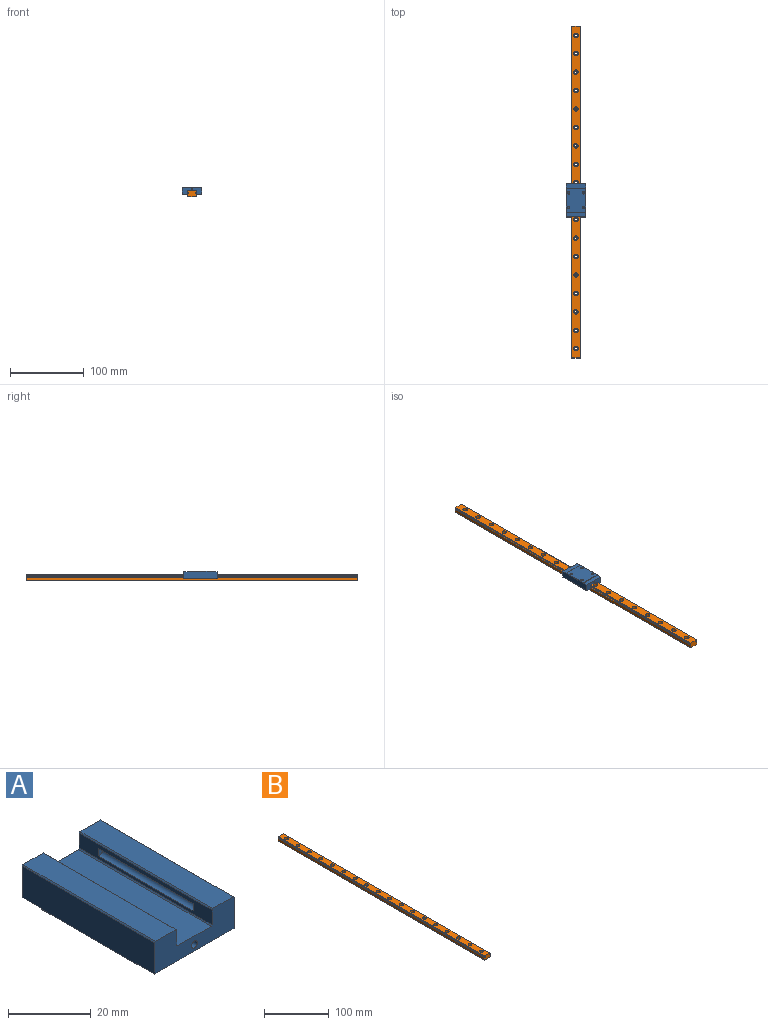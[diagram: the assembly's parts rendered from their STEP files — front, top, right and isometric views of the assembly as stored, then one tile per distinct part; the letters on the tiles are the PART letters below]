
ASSEMBLY  parts=2 mates=1
PART A: 37 faces, bbox 27x45.4x10 mm
  f0: plane 45.4x0.3mm, normal (-0.71,0,0.71), area 19.3mm2, adj f3,f6,f22,f23
  f1: plane 45.4x0.3mm, normal (0.71,0,0.71), area 19.3mm2, adj f10,f11,f22,f23
  f2: plane 45.4x0.3mm, normal (0.71,0,0.71), area 19.3mm2, adj f6,f7,f22,f23
  f3: plane 45.4x4.4mm, normal (-1,0,0), area 129.2mm2, adj f0,f5,f17,f20,f22,f23,f24
  f4: plane 45.4x11.4mm, normal (0,0,1), area 517.6mm2, adj f16,f17,f22,f23
  f5: cylinder r=1.15mm len=32.4mm, axis (0,-1,0), area 141.5mm2, adj f3,f20,f24
  f6: plane 45.4x6.9mm, normal (0,0,1), area 313.3mm2, adj f0,f2,f22,f23
  f7: plane 45.4x9.4mm, normal (1,0,0), area 424.2mm2, adj f2,f15,f18,f21,f22,f23,f25,f35
  f8: plane 32.4x26.4mm, normal (0,0,-1), area 821.1mm2, adj f14,f15,f18,f27,f29,f31,f33,f35
  f9: plane 45.4x9.4mm, normal (-1,0,0), area 424.2mm2, adj f14,f18,f21,f22,f23,f25,f34,f35
  f10: plane 45.4x6.9mm, normal (0,0,1), area 313.3mm2, adj f1,f22,f23,f34
  f11: plane 45.4x4.4mm, normal (1,0,0), area 129.2mm2, adj f1,f12,f16,f19,f22,f23,f36
  f12: cylinder r=1.15mm len=32.4mm, axis (0,-1,0), area 141.5mm2, adj f11,f19,f36
  f13: cylinder r=1mm len=45.4mm, axis (0,-1,0), area 285.3mm2, adj f22,f23
  f14: plane 32.4x0.3mm, normal (-0.71,0,-0.71), area 13.7mm2, adj f8,f9,f18,f35
  f15: plane 32.4x0.3mm, normal (0.71,0,-0.71), area 13.7mm2, adj f7,f8,f18,f35
  f16: plane 45.4x0.3mm, normal (0.71,0,0.71), area 19.3mm2, adj f4,f11,f22,f23
  f17: plane 45.4x0.3mm, normal (-0.71,0,0.71), area 19.3mm2, adj f3,f4,f22,f23
  f18: plane 27x0.5mm, normal (0,-1,0), area 13.4mm2, adj f7,f8,f9,f14,f15,f21
  f19: plane 2.3x1.52mm, normal (0,1,0), area 2.9mm2, adj f11,f12
  f20: plane 2.3x1.52mm, normal (0,1,0), area 2.9mm2, adj f3,f5
  f21: plane 27x6.5mm, normal (0,0,-1), area 175.5mm2, adj f7,f9,f18,f22
  f22: plane 27x9.5mm, normal (0,-1,0), area 193.3mm2, adj f0,f1,f2,f3,f4,f6,f7,f9
  f23: plane 27x9.5mm, normal (0,1,0), area 193.3mm2, adj f0,f1,f2,f3,f4,f6,f7,f9
  f24: plane 2.3x1.52mm, normal (0,-1,0), area 2.9mm2, adj f3,f5
  f25: plane 27x6.5mm, normal (0,0,-1), area 175.5mm2, adj f7,f9,f23,f35
  f26: cone r=857.17mm half-angle=59deg, axis (0,0,-1), area 10mm2, adj f27
  f27: cylinder r=1.65mm len=3.5mm, axis (0,0,1), area 36.3mm2, adj f8,f26
  f28: cone r=857.17mm half-angle=59deg, axis (0,0,-1), area 10mm2, adj f29
  f29: cylinder r=1.65mm len=3.5mm, axis (0,0,1), area 36.3mm2, adj f8,f28
  f30: cone r=857.17mm half-angle=59deg, axis (0,0,-1), area 10mm2, adj f31
  f31: cylinder r=1.65mm len=3.5mm, axis (0,0,1), area 36.3mm2, adj f8,f30
  f32: cone r=857.17mm half-angle=59deg, axis (0,0,-1), area 10mm2, adj f33
  f33: cylinder r=1.65mm len=3.5mm, axis (0,0,1), area 36.3mm2, adj f8,f32
  f34: plane 45.4x0.3mm, normal (-0.71,0,0.71), area 19.3mm2, adj f9,f10,f22,f23
  f35: plane 27x0.5mm, normal (0,1,0), area 13.4mm2, adj f7,f8,f9,f14,f15,f25
  f36: plane 2.3x1.52mm, normal (0,-1,0), area 2.9mm2, adj f11,f12
PART B: 76 faces, bbox 12x450x8 mm
  f0: plane 450x0.51mm, normal (0,0,1), area 229.4mm2, adj f1,f19,f20,f51
  f1: plane 450x0.3mm, normal (1,0,0), area 135mm2, adj f0,f2,f20,f51
  f2: plane 450x0.51mm, normal (0,0,-1), area 229.4mm2, adj f1,f3,f20,f51
  f3: cylinder r=1.15mm len=450mm, axis (0,1,0), area 575.7mm2, adj f2,f4,f20,f51
  f4: plane 450x0.86mm, normal (1,0,0), area 387.4mm2, adj f3,f5,f20,f51
  f5: plane 450x0.35mm, normal (0.71,0,0.71), area 222.7mm2, adj f4,f6,f20,f51
  f6: plane 450x11.3mm, normal (0,0,1), area 4576.1mm2, adj f5,f7,f20,f23,f26,f29,f32,f35
  f7: plane 450x0.35mm, normal (-0.71,0,0.71), area 222.7mm2, adj f6,f8,f20,f51
  f8: plane 450x0.86mm, normal (-1,0,0), area 387.4mm2, adj f7,f9,f20,f51
  f9: cylinder r=1.15mm len=450mm, axis (0,1,0), area 575.7mm2, adj f8,f10,f20,f51
  f10: plane 450x0.51mm, normal (0,0,-1), area 229.4mm2, adj f9,f11,f20,f51
  f11: plane 450x0.3mm, normal (-1,0,0), area 135mm2, adj f10,f12,f20,f51
  f12: plane 450x0.51mm, normal (0,0,1), area 229.4mm2, adj f11,f13,f20,f51
  f13: cylinder r=1.15mm len=450mm, axis (0,1,0), area 575.7mm2, adj f12,f14,f20,f51
  f14: plane 450x4.26mm, normal (-1,0,0), area 1917.6mm2, adj f13,f15,f20,f51
  f15: plane 450x0.35mm, normal (-0.71,0,-0.71), area 222.7mm2, adj f14,f16,f20,f51
  f16: plane 450x11.3mm, normal (0,0,-1), area 4911.8mm2, adj f15,f17,f20,f21,f24,f27,f30,f33
  f17: plane 450x0.35mm, normal (0.71,0,-0.71), area 222.7mm2, adj f16,f18,f20,f51
  f18: plane 450x4.26mm, normal (1,0,0), area 1917.6mm2, adj f17,f19,f20,f51
  f19: cylinder r=1.15mm len=450mm, axis (0,1,0), area 575.7mm2, adj f0,f18,f20,f51
  f20: plane 12x8mm, normal (0,-1,0), area 93mm2, adj f0,f1,f2,f3,f4,f5,f6,f7
  f21: cylinder r=1.75mm len=3.5mm, axis (0,0,1), area 38.5mm2, adj f16,f22
  f22: plane 6x6mm, normal (0,0,1), area 18.7mm2, adj f21,f23
  f23: cylinder r=3mm len=6mm, axis (0,0,1), area 84.8mm2, adj f6,f22
  f24: cylinder r=1.75mm len=3.5mm, axis (0,0,1), area 38.5mm2, adj f16,f25
  f25: plane 6x6mm, normal (0,0,1), area 18.7mm2, adj f24,f26
  f26: cylinder r=3mm len=6mm, axis (0,0,1), area 84.8mm2, adj f6,f25
  f27: cylinder r=1.75mm len=3.5mm, axis (0,0,1), area 38.5mm2, adj f16,f28
  f28: plane 6x6mm, normal (0,0,1), area 18.7mm2, adj f27,f29
  f29: cylinder r=3mm len=6mm, axis (0,0,1), area 84.8mm2, adj f6,f28
  f30: cylinder r=1.75mm len=3.5mm, axis (0,0,1), area 38.5mm2, adj f16,f31
  f31: plane 6x6mm, normal (0,0,1), area 18.7mm2, adj f30,f32
  f32: cylinder r=3mm len=6mm, axis (0,0,1), area 84.8mm2, adj f6,f31
  f33: cylinder r=1.75mm len=3.5mm, axis (0,0,1), area 38.5mm2, adj f16,f34
  f34: plane 6x6mm, normal (0,0,1), area 18.7mm2, adj f33,f35
  f35: cylinder r=3mm len=6mm, axis (0,0,1), area 84.8mm2, adj f6,f34
  f36: cylinder r=1.75mm len=3.5mm, axis (0,0,1), area 38.5mm2, adj f16,f37
  f37: plane 6x6mm, normal (0,0,1), area 18.7mm2, adj f36,f38
  f38: cylinder r=3mm len=6mm, axis (0,0,1), area 84.8mm2, adj f6,f37
  f39: cylinder r=1.75mm len=3.5mm, axis (0,0,1), area 38.5mm2, adj f16,f40
  f40: plane 6x6mm, normal (0,0,1), area 18.7mm2, adj f39,f41
  f41: cylinder r=3mm len=6mm, axis (0,0,1), area 84.8mm2, adj f6,f40
  f42: cylinder r=1.75mm len=3.5mm, axis (0,0,1), area 38.5mm2, adj f16,f43
  f43: plane 6x6mm, normal (0,0,1), area 18.7mm2, adj f42,f44
  f44: cylinder r=3mm len=6mm, axis (0,0,1), area 84.8mm2, adj f6,f43
  f45: cylinder r=1.75mm len=3.5mm, axis (0,0,1), area 38.5mm2, adj f16,f46
  f46: plane 6x6mm, normal (0,0,1), area 18.7mm2, adj f45,f47
  f47: cylinder r=3mm len=6mm, axis (0,0,1), area 84.8mm2, adj f6,f46
  f48: cylinder r=1.75mm len=3.5mm, axis (0,0,1), area 38.5mm2, adj f16,f49
  f49: plane 6x6mm, normal (0,0,1), area 18.7mm2, adj f48,f50
  f50: cylinder r=3mm len=6mm, axis (0,0,1), area 84.8mm2, adj f6,f49
  f51: plane 12x8mm, normal (0,1,0), area 93mm2, adj f0,f1,f2,f3,f4,f5,f6,f7
  f52: cylinder r=1.75mm len=3.5mm, axis (0,0,1), area 38.5mm2, adj f16,f53
  f53: plane 6x6mm, normal (0,0,1), area 18.7mm2, adj f52,f54
  f54: cylinder r=3mm len=6mm, axis (0,0,1), area 84.8mm2, adj f6,f53
  f55: cylinder r=1.75mm len=3.5mm, axis (0,0,1), area 38.5mm2, adj f16,f56
  f56: plane 6x6mm, normal (0,0,1), area 18.7mm2, adj f55,f57
  f57: cylinder r=3mm len=6mm, axis (0,0,1), area 84.8mm2, adj f6,f56
  f58: cylinder r=1.75mm len=3.5mm, axis (0,0,1), area 38.5mm2, adj f16,f59
  f59: plane 6x6mm, normal (0,0,1), area 18.7mm2, adj f58,f60
  f60: cylinder r=3mm len=6mm, axis (0,0,1), area 84.8mm2, adj f6,f59
  f61: cylinder r=1.75mm len=3.5mm, axis (0,0,1), area 38.5mm2, adj f16,f62
  f62: plane 6x6mm, normal (0,0,1), area 18.7mm2, adj f61,f63
  f63: cylinder r=3mm len=6mm, axis (0,0,1), area 84.8mm2, adj f6,f62
  f64: cylinder r=1.75mm len=3.5mm, axis (0,0,1), area 38.5mm2, adj f16,f65
  f65: plane 6x6mm, normal (0,0,1), area 18.7mm2, adj f64,f66
  f66: cylinder r=3mm len=6mm, axis (0,0,1), area 84.8mm2, adj f6,f65
  f67: cylinder r=1.75mm len=3.5mm, axis (0,0,1), area 38.5mm2, adj f16,f68
  f68: plane 6x6mm, normal (0,0,1), area 18.7mm2, adj f67,f69
  f69: cylinder r=3mm len=6mm, axis (0,0,1), area 84.8mm2, adj f6,f68
  f70: cylinder r=1.75mm len=3.5mm, axis (0,0,1), area 38.5mm2, adj f16,f71
  f71: plane 6x6mm, normal (0,0,1), area 18.7mm2, adj f70,f72
  f72: cylinder r=3mm len=6mm, axis (0,0,1), area 84.8mm2, adj f6,f71
  f73: cylinder r=1.75mm len=3.5mm, axis (0,0,1), area 38.5mm2, adj f16,f74
  f74: plane 6x6mm, normal (0,0,1), area 18.7mm2, adj f73,f75
  f75: cylinder r=3mm len=6mm, axis (0,0,1), area 84.8mm2, adj f6,f74
PLACE A rot(axis=(0,1,0),180deg) t=(-48.97,248.01,-21.46)mm
PLACE B t=(-48.97,43,-21.46)mm
MATE slider B.f20 <-> A.f22  axis (0,-1,0) through (-48.97,18,-21.46)mm
